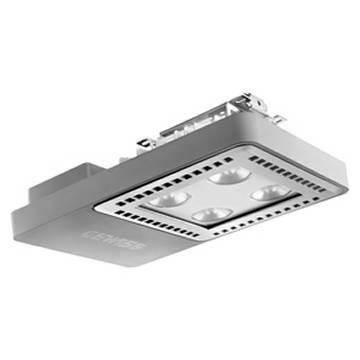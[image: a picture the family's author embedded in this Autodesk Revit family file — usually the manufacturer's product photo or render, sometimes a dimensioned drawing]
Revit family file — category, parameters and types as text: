
# Revit family: Lighting-Industriale-GEWISS-SMART[4]HLO_APPARECCHI-LED_EMERGENZA_1M
name_source: partatom
category: Apparecchi per illuminazione
units: mm (PartAtom-declared; Revit-internal decimal feet)

## family parameters
Basato su piano di lavoro = Sì
Condiviso = No
Numero OmniClass = 23.80.00.00
Punto di calcolo locali = No
Quota connettore circolare = Usa diametro
Sempre verticale = No
Sorgente d'illuminazione = No
Taglio con vuoti quando caricato = No
Tipo di parte = Normale
Titolo OmniClass = Electric Power and Lighting

## types (1)
- Lighting-Industriale-GEWISS-SMART[4]HLO_APPARECCHI-LED_EMERGENZA_1M
    Alimentatore = Incluso
    Apparecchio a ridotta temperatura superficiale = Si
    Applicazione = Interno
    Cablaggio = Con connettore stagno Gw connect
    Caratteristiche elettriche e gestione della luce = -
    Caratteristiche ottiche e illuminotecniche = -
    Carico apparente = 50 VA
    Catalogo = LIGHTING
    Certificazione DIN 18032-3 = -
    Certificazioni e classificazioni = -
    Classe fotobiologica = RG0
    Classe isolamento = I
    Classificazione = Lighting
    Classificazione: = -
    Codice Electrocod = 2444
    Codice digitale univoco (Datamatrix) = Datamatrix
    Colore = Grigio RAL 7035
    Commenti sul wattaggio = 50W
    Contesto = Illuminazione di logistiche e locali produttivi industriali
    Controllo abbagliamento e luminanza = -
    Corpo = PA6 “Halogen Free” caricato fibra vetro
    Descrizione = SMART[4]LB 1M EMERG.HLO ELL.57K
    Dispositivo di protezione = DM 6 kV / CM 10 kV
    Distanza tot_plafoniera = 74 mm  [stored 0.242782 ft]
    Durata di vita = L90B10 (Tq+25°C) = 100.000 h - L90B10 (Tq+50°C) = 50.000 h
    Efficienza luminosa (lm/W) = 119
    Finitura colore = Grigio RAL 7035
    Fissaggio = -
    Flusso luminoso apparecchio (lm) = 8200 (750 Emerg.)
    Frequenza nominale (Hz) = 50/60 Hz
    Gancio di chiusura = -
    Garanzia = 5 anni
    Grado di protezione = IP65
    Gruppo ottico = Riflettore in PC metallizzato e lenti in PMMA
    Guarnizioni = tipo siliconico antinvecchiamento
    IDF = 8dc7f14d-976c-4b7f-be5c-8ef1cd52bafa
    IDT = dbfa2a0d0d304b5c9c716a8a975efb61
    IPEA = -
    Immagine tipo = GWL1071.jpg
    Inclinazione = -
    Indice di resa cromatica = CRI-80
    Informazioni generali = -
    Installazione e manutenzione = -
    Lampada = LED
    Larghezza = 253 mm  [stored 0.830052 ft]
    Lunghezza = 383 mm  [stored 1.25656 ft]
    Materiali = -
    Modello = GWS4124BQ857
    Motore = <Per categoria>
    Norma di riferimento = EN 60598-2-22 ; EN 60598-1 ; EN 60598-2-24
    Ottica = Ellittica
    Peso (kg): = 5
    Plafoniera = <Per categoria>
    Potenza assorbita : = 64 W (+5W Emerg.)
    Produttore = GEWISS S.p.A.
    Prospetto di default = 1219 mm
    Raggio led = 30 mm  [stored 0.0984252 ft]
    Resistenza agli urti = IK08
    Resistenza al filo incandescente = 850 °C
    Scheda Tecnica = https://www.gewiss.com
    Schermo = Vetro Temprato Spessore 4mm
    Sistema di controllo = 1 x DALI DT6 + 1 x DALI DT1 (Emerg. 3h)
    Sostituibilità gruppo ottico = Non sostituibile
    Sostituibilità piastra di cablaggio = Solo batteria NiMh
    Spessore plafoniera = 40 mm  [stored 0.131234 ft]
    Superficie massima esposta al vento : = 0,140 m²
    Temperatura di colore = 5700K
    Temperatura di esercizio = 0 ÷ +40 °C
    Temperatura di stoccaggio = -40 +70 °C
    Tensione di alimentazione = 220 - 240 V
    Tipo di apparecchio = Riflettore industriale a LED&nbsp;
    Tipo di installazione e montaggio = Plafone - Sospensione
    Tipologia sorgente luminosa = LED - Non sostituibile
    Tolleranza cromatica = SDCM = 3
    Trasformatore = <Per categoria>
    URL = https://www.gewiss.com
    Vano di alimentazione = Integrato
    Versione file RFA = 20.11
    Vetro acceso = Lampada accesa
    Viti esterne = Acciaio inox
    Voltaggio = 230 V

note: [stored X ft] marks values corroborated as IEEE doubles in the binary element streams (Revit-internal decimal feet)

## geometry (parser evidence)
native form markers: Blend x4
no freeform markers — native parametric forms only
